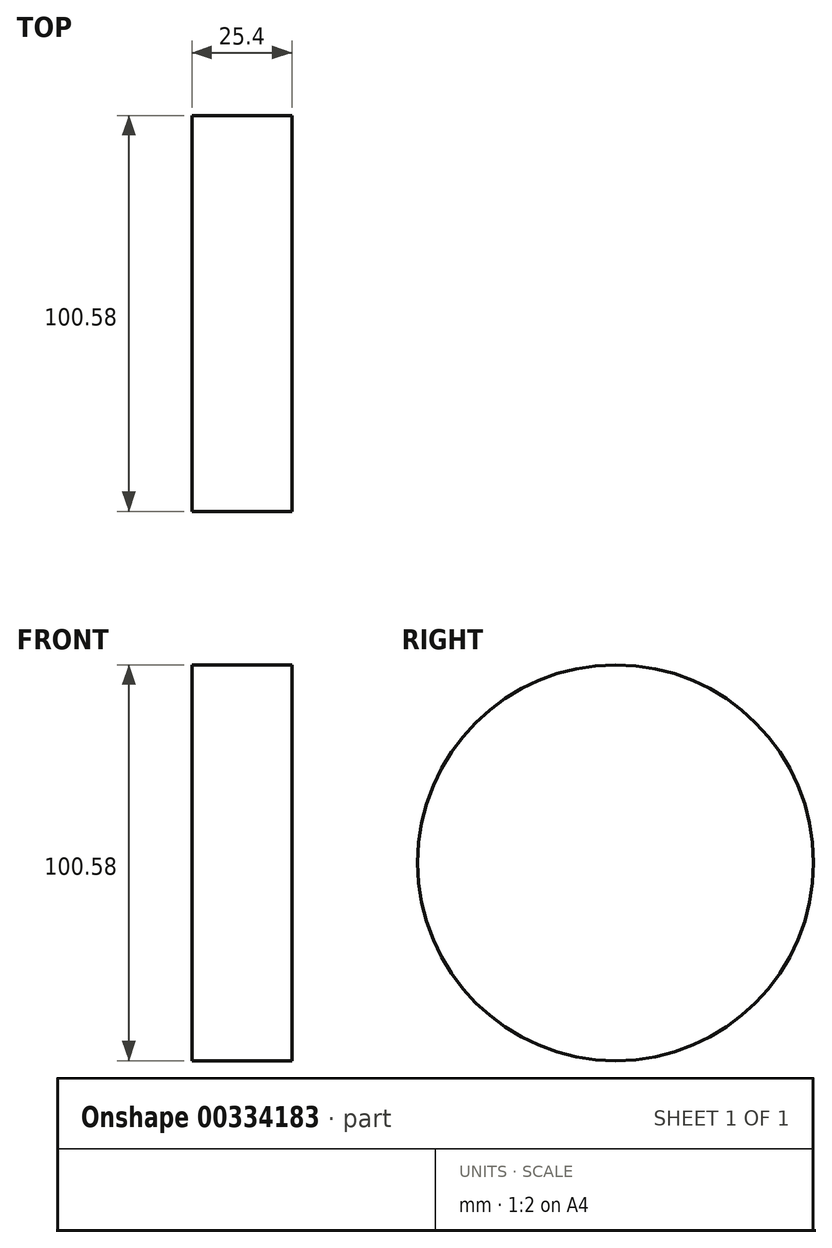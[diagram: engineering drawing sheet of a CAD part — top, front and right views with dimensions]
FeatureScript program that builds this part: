
annotation { "Feature Type Name" : "Feature", "Feature Type Description" : "" }
export const myFeature = defineFeature(function(context is Context, id is Id, definition is map)
    precondition{}
    {
        {
            var Q0;
            Q0=qCreatedBy(makeId("Right.planeOp"),FACE);
            var sketch = newSketch(context, id + "F0", { "sketchPlane" : qUnion([Q0])});
            skCircle(sketch, "E0", {"center": v(0, 0) * mm, "radius": 50.3 * mm});
            skSolve(sketch);
        }
        {
            var Q0;
            Q0=makeQuery(id+"F0.imprint","IMPRINT",FACE,{"disambiguationData":[TD([[makeQuery(id+"F0.imprint","IMPRINT",EDGE,{"derivedFrom":sQuery(id+"F0.wireOp",EDGE,"E0")}),1.0]])]});
            extrude(context, id + "F1", {"entities" : qUnion([Q0]), "depth" : 25.4 * mm});
        }
    });
